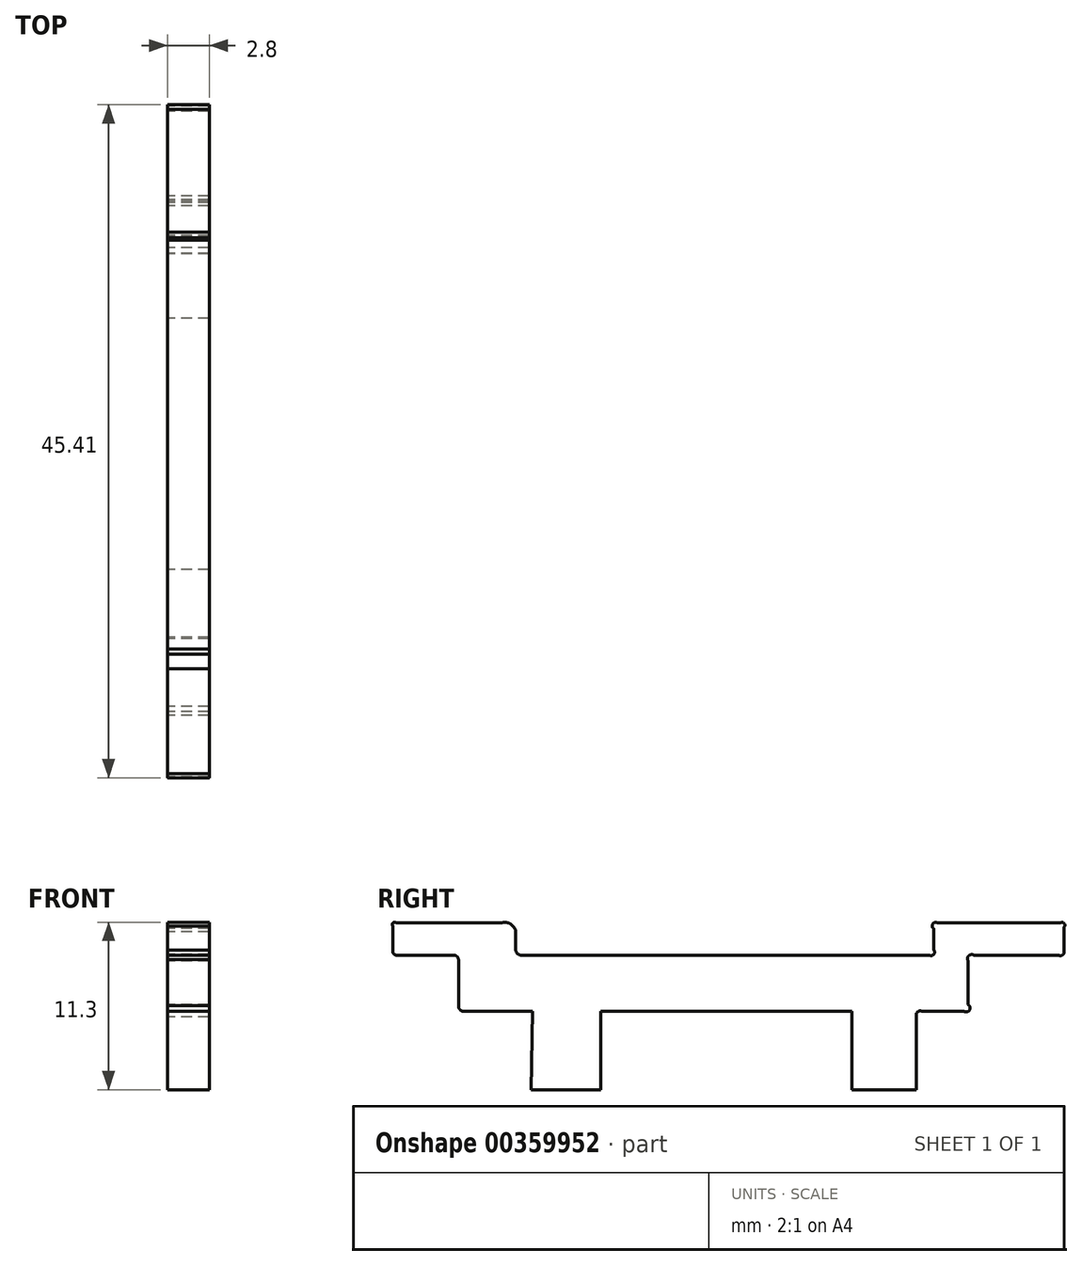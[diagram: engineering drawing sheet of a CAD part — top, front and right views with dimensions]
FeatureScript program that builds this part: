
annotation { "Feature Type Name" : "Feature", "Feature Type Description" : "" }
export const myFeature = defineFeature(function(context is Context, id is Id, definition is map)
    precondition{}
    {
        {
            var Q0;
            Q0=qCreatedBy(makeId("Right.planeOp"),FACE);
            var sketch = newSketch(context, id + "F0", { "sketchPlane" : qUnion([Q0])});
            skLineSegment(sketch, "E0", {"start": v(-26.2, 0) * mm, "end": v(-21.52, 0) * mm});
            skLineSegment(sketch, "E1", {"start": v(-21.52, 0) * mm, "end": v(-21.52, 5.28) * mm});
            skLineSegment(sketch, "E2", {"start": v(-21.52, 5.28) * mm, "end": v(-4.56, 5.28) * mm});
            skLineSegment(sketch, "E3", {"start": v(-4.56, 5.28) * mm, "end": v(-4.56, 0) * mm});
            skLineSegment(sketch, "E4", {"start": v(-4.56, 0) * mm, "end": v(-0.2, 0) * mm});
            skLineSegment(sketch, "E5", {"start": v(-0.2, 0) * mm, "end": v(-0.2, 4.92) * mm});
            skLineSegment(sketch, "E6", {"start": v(0.18, 5.28) * mm, "end": v(3.02, 5.28) * mm});
            skLineSegment(sketch, "E7", {"start": v(3.3, 5.73) * mm, "end": v(3.3, 8.67) * mm});
            skLineSegment(sketch, "E8", {"start": v(9.53, 11.25) * mm, "end": v(2.26, 11.25) * mm});
            skLineSegment(sketch, "E9", {"start": v(2.26, 11.25) * mm, "end": v(1.23, 11.25) * mm});
            skLineSegment(sketch, "E10", {"start": v(0.97, 10.87) * mm, "end": v(0.97, 9.44) * mm});
            skLineSegment(sketch, "E11", {"start": v(-27.24, 9.4) * mm, "end": v(-27.24, 10.65) * mm});
            skLineSegment(sketch, "E12", {"start": v(-27.74, 11.25) * mm, "end": v(-35.3, 11.25) * mm});
            skLineSegment(sketch, "E13", {"start": v(-35.54, 11.05) * mm, "end": v(-35.54, 9.28) * mm});
            skLineSegment(sketch, "E14", {"start": v(-35.3, 9.07) * mm, "end": v(-31.36, 9.07) * mm});
            skLineSegment(sketch, "E15", {"start": v(-31.1, 8.78) * mm, "end": v(-31.1, 5.64) * mm});
            skLineSegment(sketch, "E16", {"start": v(-30.75, 5.28) * mm, "end": v(-26.11, 5.28) * mm});
            skLineSegment(sketch, "E17", {"start": v(-26.11, 5.28) * mm, "end": v(-26.2, 0) * mm});
            skArc(sketch, "E18", {"start": v(-27.24, 10.65) * mm, "mid": v(-27.6, 11.18) * mm, "end": v(-28.23, 11.25) * mm});
            skArc(sketch, "E19", {"start": v(-31.1, 8.71) * mm, "mid": v(-31.22, 9) * mm, "end": v(-31.52, 9.07) * mm});
            skArc(sketch, "E20", {"start": v(-27.24, 9.5) * mm, "mid": v(-27.15, 9.2) * mm, "end": v(-26.86, 9.07) * mm});
            skPoint(sketch, "E21.orphan", {"position": v(-27.24, 11.25) * mm});
            skArc(sketch, "E22", {"start": v(-31.1, 5.67) * mm, "mid": v(-31.01, 5.4) * mm, "end": v(-30.75, 5.28) * mm});
            skArc(sketch, "E23", {"start": v(-35.54, 9.41) * mm, "mid": v(-35.5, 9.19) * mm, "end": v(-35.3, 9.07) * mm});
            skArc(sketch, "E24", {"start": v(-35.3, 11.25) * mm, "mid": v(-35.52, 11.27) * mm, "end": v(-35.54, 11.05) * mm});
            skPoint(sketch, "E25.orphan", {"position": v(-35.54, 11.25) * mm});
            skPoint(sketch, "E26.orphan", {"position": v(-35.54, 9.07) * mm});
            skPoint(sketch, "E27.orphan", {"position": v(-31.1, 5.28) * mm});
            skArc(sketch, "E28", {"start": v(0.18, 5.28) * mm, "mid": v(-0.13, 5.24) * mm, "end": v(-0.2, 4.92) * mm});
            skArc(sketch, "E29", {"start": v(3.02, 5.28) * mm, "mid": v(3.39, 5.36) * mm, "end": v(3.3, 5.73) * mm});
            skArc(sketch, "E30", {"start": v(3.69, 9.07) * mm, "mid": v(3.33, 9.03) * mm, "end": v(3.3, 8.67) * mm});
            skArc(sketch, "E31", {"start": v(9.4, 9.07) * mm, "mid": v(9.7, 9.1) * mm, "end": v(9.75, 9.4) * mm});
            skArc(sketch, "E32", {"start": v(9.75, 10.95) * mm, "mid": v(9.8, 11.21) * mm, "end": v(9.53, 11.25) * mm});
            skArc(sketch, "E33", {"start": v(1.23, 11.25) * mm, "mid": v(0.9, 11.19) * mm, "end": v(0.97, 10.87) * mm});
            skArc(sketch, "E34", {"start": v(0.68, 9.07) * mm, "mid": v(0.98, 9.14) * mm, "end": v(0.97, 9.44) * mm});
            skLineSegment(sketch, "E35.trimOffspring", {"start": v(0.68, 9.07) * mm, "end": v(-26.88, 9.07) * mm});
            skPoint(sketch, "E36.trimOffspring.end.orphan", {"position": v(0.97, 9.07) * mm});
            skLineSegment(sketch, "E37.trimOffspring", {"start": v(9.75, 9.4) * mm, "end": v(9.75, 10.95) * mm});
            skLineSegment(sketch, "E38", {"start": v(3.69, 9.07) * mm, "end": v(9.4, 9.07) * mm});
            skPoint(sketch, "E39.start.orphan", {"position": v(9.75, 9.07) * mm});
            skPoint(sketch, "E40.orphan", {"position": v(-0.2, 5.28) * mm});
            skSolve(sketch);
        }
        {
            var Q0;
            Q0 = qSketchRegion(id + "F0", true);
            extrude(context, id + "F1", {"entities" : qUnion([Q0]), "depth" : 2.8 * mm});
        }
    });
